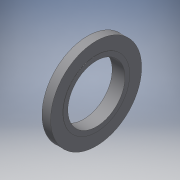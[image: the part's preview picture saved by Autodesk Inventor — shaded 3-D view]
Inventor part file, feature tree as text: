
AUTODESK INVENTOR PART (.ipt)
format: ipt  version: 2017.3 (Build 213257000, 257)  size: 152,576 bytes
history: native  units: in
note: dims shown in document units (in); Inventor stores cm internally (conversion verified against a paired STEP export)
features: revolve x2, sketch x2, projected_geometry x1
ambient origin geometry x8: Origin, YZ Plane, XZ Plane, XY Plane, X Axis, Y Axis, Z Axis, Center Point
bodies: Solid1 (feature_tree)
feature tree (5):
  revolve  "Revolution1"  [1 undecoded]
  revolve  "Revolution2"  [1 undecoded]
  sketch  "Sketch1"  dims[d0=0.0625in d2=1.94in]
  sketch  "Sketch2"  dims[d3=10.25in d4=7.5in d5=6.44in d6=7.375in d7=2.82in d8=90.0deg d9=90.0deg d10=0.0625in d11=0.2577in d12=7.0in d13=1.0in d14=6.3125in d15=6.5in d16=0.875in d17=90.0deg]
  projected_geometry  "Project Cut Edges1"
note: 2 required parameter values undecoded (feature->parameter linkage not recoverable at this tier; creation-order binding heuristic only, values carry confidence <= 0.55)
